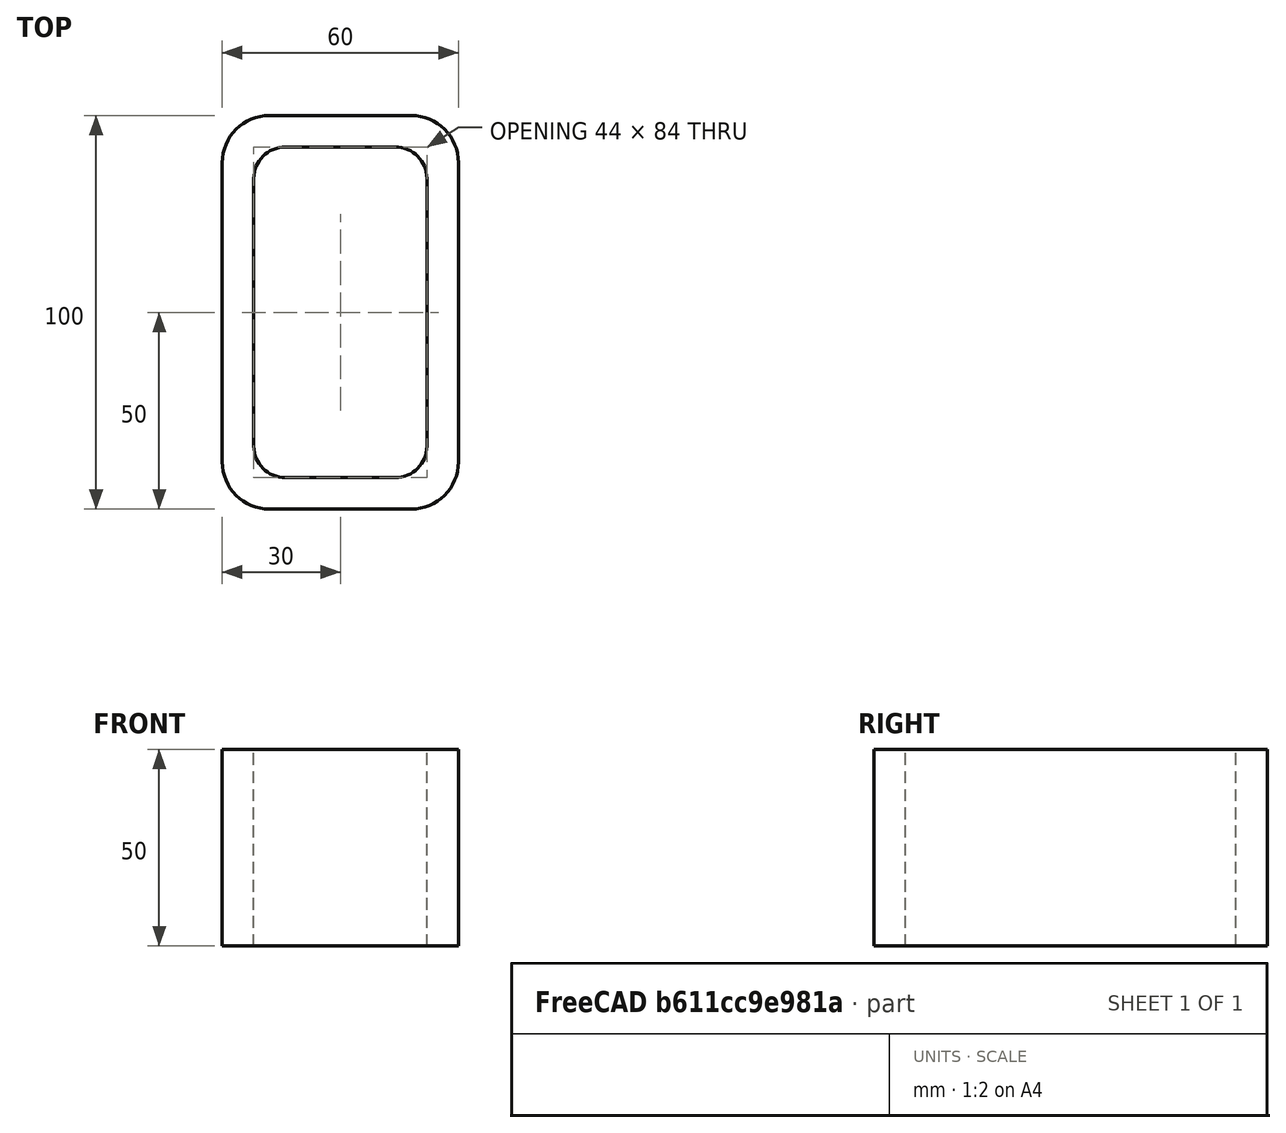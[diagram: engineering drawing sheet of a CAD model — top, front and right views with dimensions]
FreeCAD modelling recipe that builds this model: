
FCSTD DOCUMENT  (FreeCAD 0.15R4671 (Git))
Label: Rectangular hollow section 100x60x8 EN10219 S235JRH
License: All rights reserved
LicenseURL: http://en.wikipedia.org/wiki/All_rights_reserved
objects: Sketcher::SketchObject×1, Part::Extrusion×1
note: 2 computed .brp shape members not serialized (recipe doc carries the construction recipe); baked Part::Feature solids carry a one-line shape summary decoded from their .brp

FEATURE [Sketcher::SketchObject] Sketch
  sketch-geometry (16):
    g0: LineSegment StartX=-14 StartY=42 StartZ=0 EndX=14 EndY=42 EndZ=0
    g1: LineSegment StartX=22 StartY=34 StartZ=0 EndX=22 EndY=-34 EndZ=0
    g2: LineSegment StartX=14 StartY=-42 StartZ=0 EndX=-14 EndY=-42 EndZ=0
    g3: LineSegment StartX=-22 StartY=-34 StartZ=0 EndX=-22 EndY=34 EndZ=0
    g4: LineSegment StartX=-18 StartY=50 StartZ=0 EndX=18 EndY=50 EndZ=0
    g5: LineSegment StartX=30 StartY=38 StartZ=0 EndX=30 EndY=-38 EndZ=0
    g6: LineSegment StartX=18 StartY=-50 StartZ=0 EndX=-18 EndY=-50 EndZ=0
    g7: LineSegment StartX=-30 StartY=-38 StartZ=0 EndX=-30 EndY=38 EndZ=0
    g8: ArcOfCircle CenterX=-14 CenterY=34 CenterZ=0 NormalX=0 NormalY=0 NormalZ=1 Radius=8 StartAngle=1.5708 EndAngle=3.14159
    g9: ArcOfCircle CenterX=14 CenterY=34 CenterZ=0 NormalX=0 NormalY=0 NormalZ=1 Radius=8 StartAngle=0 EndAngle=1.5708
    g10: ArcOfCircle CenterX=14 CenterY=-34 CenterZ=0 NormalX=0 NormalY=0 NormalZ=1 Radius=8 StartAngle=4.71239 EndAngle=6.28319
    g11: ArcOfCircle CenterX=-14 CenterY=-34 CenterZ=0 NormalX=0 NormalY=0 NormalZ=1 Radius=8 StartAngle=3.14159 EndAngle=4.71239
    g12: ArcOfCircle CenterX=18 CenterY=38 CenterZ=0 NormalX=0 NormalY=0 NormalZ=1 Radius=12 StartAngle=0 EndAngle=1.5708
    g13: ArcOfCircle CenterX=18 CenterY=-38 CenterZ=0 NormalX=0 NormalY=0 NormalZ=1 Radius=12 StartAngle=4.71239 EndAngle=6.28319
    g14: ArcOfCircle CenterX=-18 CenterY=-38 CenterZ=0 NormalX=0 NormalY=0 NormalZ=1 Radius=12 StartAngle=3.14159 EndAngle=4.71239
    g15: ArcOfCircle CenterX=-18 CenterY=38 CenterZ=0 NormalX=0 NormalY=0 NormalZ=1 Radius=12 StartAngle=1.5708 EndAngle=3.14159
  constraints (36):
    c: Horizontal(g2)
    c: Vertical(g3)
    c: Horizontal(g6)
    c: Vertical(g7)
    c: Tangent(g3,g8) = 1.5708
    c: Tangent(g0,g8) = 1.5708
    c: Tangent(g0,g9) = 1.5708
    c: Tangent(g1,g9) = 1.5708
    c: Tangent(g1,g10) = 1.5708
    c: Tangent(g2,g10) = 1.5708
    c: Tangent(g2,g11) = 1.5708
    c: Tangent(g3,g11) = 1.5708
    c: Tangent(g4,g12) = 1.5708
    c: Tangent(g5,g12) = 1.5708
    c: Tangent(g5,g13) = 1.5708
    c: Tangent(g6,g13) = 1.5708
    c: Tangent(g6,g14) = 1.5708
    c: Tangent(g7,g14) = 1.5708
    c: Tangent(g7,g15) = 1.5708
    c: Tangent(g4,g15) = 1.5708
    c: Equal(g9,g8)
    c: Equal(g9,g11)
    c: Equal(g9,g10)
    c: Equal(g12,g15)
    c: Equal(g12,g14)
    c: Equal(g12,g13)
    c: Symmetric(g4,g6,g-1)
    c: Symmetric(g7,g5,g-2)
    c: DistanceY(g4,g6) = -100
    c: DistanceX(g7,g5) = 60
    c: Symmetric(g3,g1,g-2)
    c: Symmetric(g0,g2,g-1)
    c: DistanceY(g0,g4) = 8
    c: DistanceX(g5,g1) = -8
    c: Radius(g9) = 8
    c: Radius(g12) = 12
FEATURE [Part::Extrusion] Extrude  label="Rectangular hollow section 100x60x8 EN10219 S235JRH"
  Base = -> Sketch
  Dir = (0,0,50)
  Solid = true
